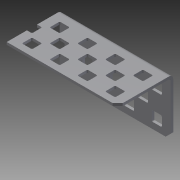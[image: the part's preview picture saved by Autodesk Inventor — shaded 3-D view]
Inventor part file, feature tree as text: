
AUTODESK INVENTOR PART (.ipt)
format: ipt  version: 2014 SP1 (Build 180222100, 222)  size: 830,464 bytes
history: native  units: in
note: dims shown in document units (in); Inventor stores cm internally (conversion verified against a paired STEP export)
features: other x1, imported_body x1, extrude x1, sketch x1
ambient origin geometry x8: Origin, YZ Plane, XZ Plane, XY Plane, X Axis, Y Axis, Z Axis, Center Point
bodies: Body1 (feature_tree)
feature tree (4):
  parser-record x1  (decoder bookkeeping rows leaked as tree rows — omitted from the tree; the rows remain in map.json)
  imported_body  "Base1"
  extrude  "Extrusion1"  Depth=1.0in
  sketch  "Sketch1"  dims[d0=1.0in d1=0.0in d2=5.5in]
